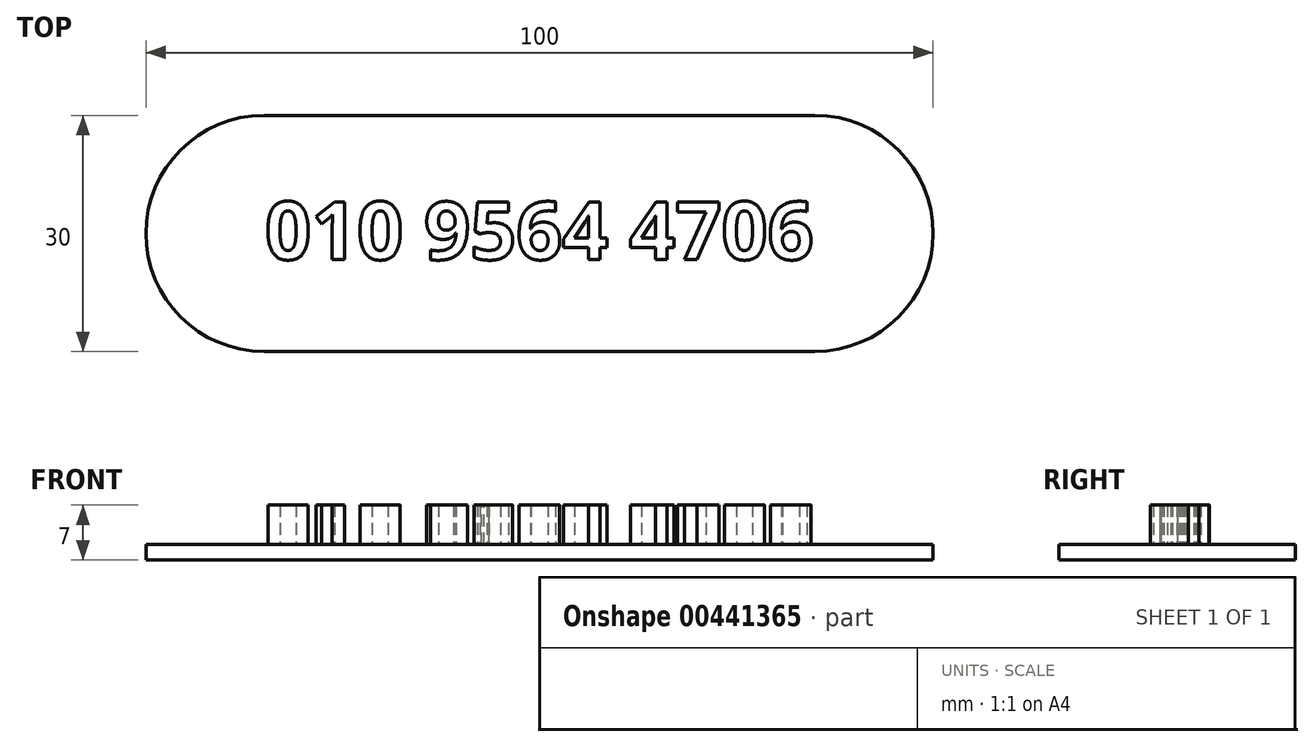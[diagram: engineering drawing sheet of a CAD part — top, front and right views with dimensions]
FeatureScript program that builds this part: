
annotation { "Feature Type Name" : "Feature", "Feature Type Description" : "" }
export const myFeature = defineFeature(function(context is Context, id is Id, definition is map)
    precondition{}
    {
        {
            var Q0;
            Q0=qCreatedBy(makeId("Top.planeOp"),FACE);
            var sketch = newSketch(context, id + "F0", { "sketchPlane" : qUnion([Q0])});
            skLineSegment(sketch, "E0.bottom", {"start": v(35, -15) * mm, "end": v(-35, -15) * mm});
            skLineSegment(sketch, "E0.top", {"start": v(35, 15) * mm, "end": v(-35, 15) * mm});
            skLineSegment(sketch, "E0.left", {"start": v(35, -15) * mm, "end": v(35, 15) * mm});
            skLineSegment(sketch, "E0.right", {"start": v(-35, -15) * mm, "end": v(-35, 15) * mm});
            skPoint(sketch, "E0.middle", {"position": v(0, 0) * mm});
            skCircle(sketch, "E1", {"center": v(-35, 0) * mm, "radius": 15 * mm});
            skCircle(sketch, "E2", {"center": v(35, 0) * mm, "radius": 15 * mm});
            skSolve(sketch);
        }
        {
            var Q0;
            Q0=qSketchRegion(id+"F0",true);
            extrude(context, id + "F1", {"entities" : qUnion([Q0]), "oppositeDirection" : true, "depth" : 2 * mm});
        }
        {
            var Q0;
            Q0=makeQuery(id+"F1.opExtrude","CAP_FACE",FACE,{"disambiguationData":[OSD([sQuery(id+"F0.wireOp",EDGE,"E0.bottom"),sQuery(id+"F0.wireOp",EDGE,"E0.top"),sQuery(id+"F0.wireOp",EDGE,"E1"),sQuery(id+"F0.wireOp",EDGE,"E2")])],"isStart":true});
            var sketch = newSketch(context, id + "F2", { "sketchPlane" : qUnion([Q0])});
            skText(sketch, "E3", { "text": "010 9564 4706", "fontName": "OpenSans-Bold.ttf"});
            const initialGuessF2  = {"E3": [-0.03487, -0.00331, 1, 0, 0.00738]};
            skSetInitialGuess(sketch, initialGuessF2);
            skSolve(sketch);
        }
        {
            var Q0;
            Q0=qSketchRegion(id+"F2",true);
            extrude(context, id + "F3", {"entities" : qUnion([Q0]), "operationType" : NewBodyOperationType.ADD, "depth" : 5 * mm});
        }
    });
